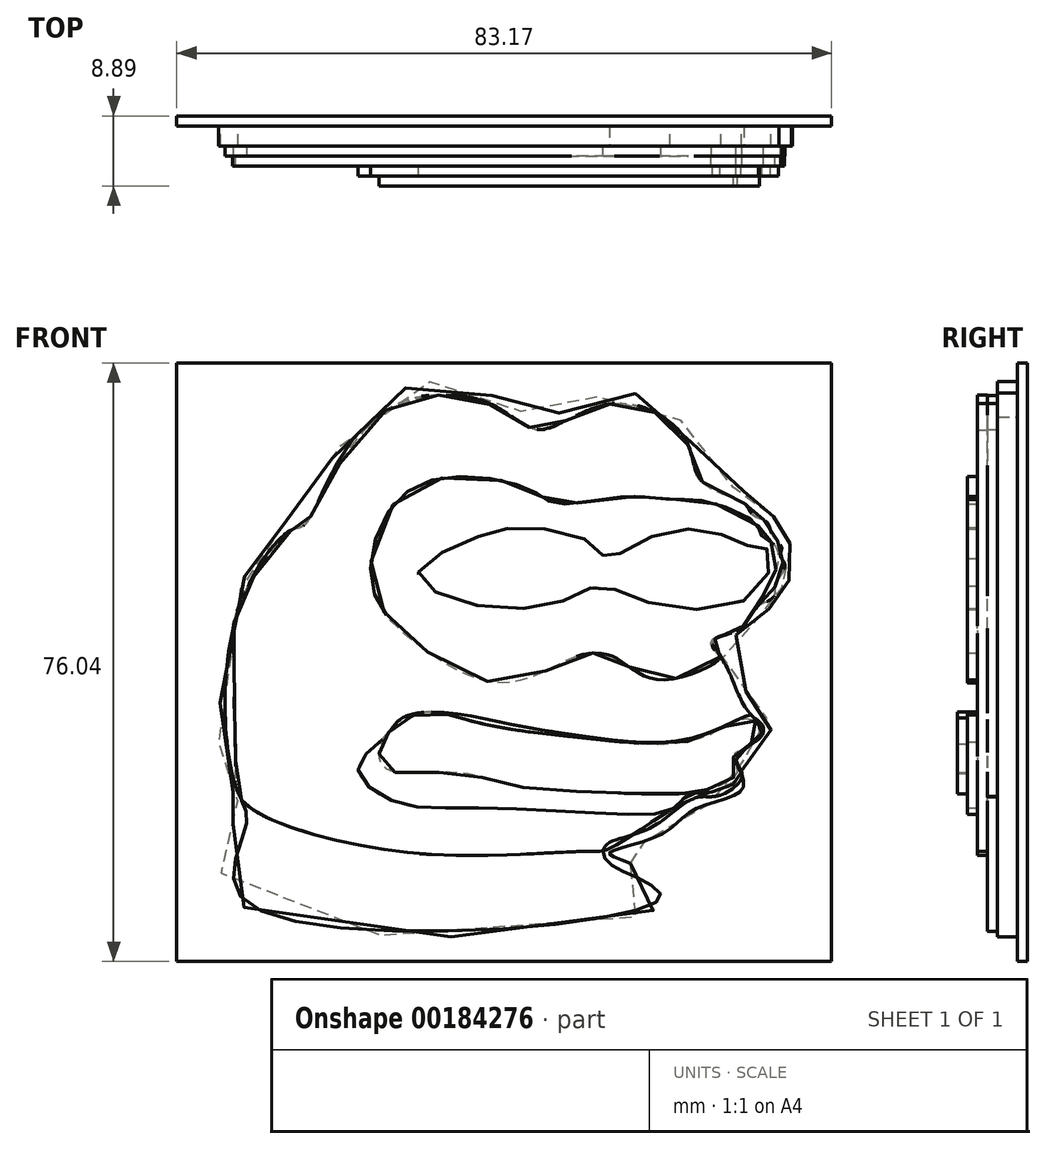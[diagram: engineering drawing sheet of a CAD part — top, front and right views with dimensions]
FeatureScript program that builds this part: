
annotation { "Feature Type Name" : "Feature", "Feature Type Description" : "" }
export const myFeature = defineFeature(function(context is Context, id is Id, definition is map)
    precondition{}
    {
        {
            var Q0;
            Q0=qCreatedBy(makeId("Front.planeOp"),FACE);
            var sketch = newSketch(context, id + "F0", { "sketchPlane" : qUnion([Q0])});
            skFitSpline(sketch, "E0", {"points": [v(8, -18.43) * mm, v(5.33, -17.05) * mm, v(11.68, -14.84) * mm, v(16.43, -11.4) * mm, v(22.25, -8.91) * mm, v(22.15, -5.68) * mm, v(25.7, -2.23) * mm, v(25.32, 0) * mm, v(24.4, 1.42) * mm, v(19.51, 9.3) * mm, v(23.44, 11.4) * mm, v(24.13, 12.87) * mm, v(26.85, 14.85) * mm, v(27, 16.2) * mm, v(28.38, 17.9) * mm, v(28.35, 20.42) * mm, v(28.25, 22.22) * mm, v(26.83, 23.31) * mm, v(26.67, 25.3) * mm, v(24.58, 26.28) * mm, v(23.94, 27.85) * mm, v(17.93, 31.16) * mm, v(13.41, 39.13) * mm, v(4.14, 40.92) * mm, v(-3.5, 38.31) * mm, v(-12.1, 42.14) * mm, v(-24.11, 40.06) * mm, v(-33.8, 27) * mm, v(-38.3, 22.43) * mm, v(-41.8, 15.7) * mm, v(-43.63, -8.1) * mm, v(-41.95, -9.82) * mm, v(-41.96, -10.5) * mm, v(-42.26, -12.67) * mm, v(-42.26, -23.19) * mm, v(12.68, -23.19) * mm, v(8, -18.43) * mm]});
            skSolve(sketch);
        }
        {
            var Q0;
            Q0 = qSketchRegion(id + "F0", true);
            extrude(context, id + "F1", {"entities" : qUnion([Q0]), "depth" : 2.54 * mm});
        }
        {
            var Q0;
            Q0=makeQuery(id+"F1.opExtrude","CAP_FACE",FACE,{"disambiguationData":[OSD([sQuery(id+"F0.wireOp",EDGE,"E0")])],"isStart":false});
            var sketch = newSketch(context, id + "F2", { "sketchPlane" : qUnion([Q0])});
            skFitSpline(sketch, "E1", {"points": [v(-33.38, 24.65) * mm, v(-25.5, 37.37) * mm, v(-10.06, 40.08) * mm, v(-3.7, 36.7) * mm, v(5.5, 39.96) * mm, v(14.93, 35.51) * mm, v(17.07, 30.08) * mm, v(22.74, 27.06) * mm, v(23.51, 25.83) * mm, v(25.27, 24.96) * mm, v(26.1, 23.08) * mm, v(27.19, 21.72) * mm, v(27, 20.66) * mm, v(27.6, 19.47) * mm, v(26.38, 16.98) * mm, v(26.1, 15.4) * mm, v(23.77, 13.98) * mm, v(21.96, 11.45) * mm, v(18.34, 9.98) * mm, v(19.18, 8.31) * mm, v(21.94, 2.3) * mm, v(23.3, 0.49) * mm, v(24.81, -1.9) * mm, v(21.39, -4.97) * mm, v(22.16, -7.13) * mm, v(19.2, -9.8) * mm, v(16.09, -10.11) * mm, v(10.35, -13.98) * mm, v(4.86, -16.1) * mm, v(4.74, -17.82) * mm, v(8.67, -20.17) * mm, v(11.6, -23.06) * mm, v(-40.87, -23.34) * mm, v(-40.82, -13.42) * mm, v(-42.17, -8.63) * mm, v(-42.07, 12.99) * mm, v(-35.07, 23.98) * mm, v(-33.38, 24.65) * mm]});
            skSolve(sketch);
        }
        {
            var Q0;
            Q0 = qSketchRegion(id + "F2", true);
            extrude(context, id + "F3", {"entities" : qUnion([Q0]), "operationType" : NewBodyOperationType.ADD, "depth" : 1.27 * mm});
        }
        {
            var Q0;
            Q0=makeQuery(id+"F3.opExtrude","CAP_FACE",FACE,{"disambiguationData":[OSD([sQuery(id+"F2.wireOp",EDGE,"E1")])],"isStart":false});
            var sketch = newSketch(context, id + "F4", { "sketchPlane" : qUnion([Q0])});
            skFitSpline(sketch, "E2", {"points": [v(-41.45, -10.34) * mm, v(-29.72, -15.39) * mm, v(-12.36, -17.43) * mm, v(2.82, -16.88) * mm, v(4.5, -16.82) * mm, v(8.25, -14.78) * mm, v(15.37, -10.45) * mm, v(22.15, -6.99) * mm, v(21.35, -5.18) * mm, v(24.86, -1.48) * mm, v(23.04, 0.73) * mm, v(19.87, 7.07) * mm, v(18.27, 9.76) * mm, v(21.94, 11.43) * mm, v(23.57, 13.76) * mm, v(26.19, 15.53) * mm, v(26.4, 17.05) * mm, v(27.5, 19) * mm, v(27, 20.72) * mm, v(27.01, 22.06) * mm, v(25.92, 23.47) * mm, v(25.2, 25.03) * mm, v(23.32, 26.06) * mm, v(22.48, 27.26) * mm, v(17.08, 30.06) * mm, v(15.5, 34.2) * mm, v(11.65, 38.54) * mm, v(5.92, 40) * mm, v(0, 37.94) * mm, v(-3.92, 36.7) * mm, v(-8.45, 39.23) * mm, v(-15.47, 41.04) * mm, v(-23.54, 38.82) * mm, v(-31.7, 27.6) * mm, v(-33.56, 24.5) * mm, v(-34.9, 24.04) * mm, v(-40.63, 16.77) * mm, v(-42.5, 11.35) * mm, v(-42.42, 8.38) * mm, v(-42.35, 1.27) * mm, v(-42.21, -6.13) * mm, v(-41.45, -10.34) * mm]});
            skSolve(sketch);
        }
        {
            var Q0;
            Q0 = qSketchRegion(id + "F4", true);
            extrude(context, id + "F5", {"entities" : qUnion([Q0]), "operationType" : NewBodyOperationType.ADD, "depth" : 1.27 * mm});
        }
        {
            var Q0;
            Q0=makeQuery(id+"F5.opExtrude","CAP_FACE",FACE,{"disambiguationData":[OSD([sQuery(id+"F4.wireOp",EDGE,"E2")])],"isStart":false});
            var sketch = newSketch(context, id + "F6", { "sketchPlane" : qUnion([Q0])});
            skFitSpline(sketch, "E3", {"points": [v(23.29, 0.46) * mm, v(16.19, -2.4) * mm, v(3.67, -2.47) * mm, v(-5.95, -0.99) * mm, v(-15.7, 0.76) * mm, v(-21.1, 0) * mm, v(-23.31, -2.47) * mm, v(-26.6, -6.24) * mm, v(-22.3, -10.48) * mm, v(-11.74, -11.35) * mm, v(6.43, -12.16) * mm, v(13.48, -11.4) * mm, v(15.25, -9.74) * mm, v(17.94, -9.4) * mm, v(22.02, -7.32) * mm, v(21.38, -5.08) * mm, v(24.65, -1.84) * mm, v(23.81, 0) * mm, v(23.29, 0.46) * mm]});
            skFitSpline(sketch, "E4", {"points": [v(19.35, 7.8) * mm, v(11.88, 4.9) * mm, v(6.31, 7.56) * mm, v(1.42, 7.98) * mm, v(-8.04, 4.51) * mm, v(-19.98, 10.14) * mm, v(-24.91, 17.22) * mm, v(-21.75, 27.64) * mm, v(-12.44, 30.74) * mm, v(-4, 28.67) * mm, v(-1.58, 27.31) * mm, v(7.38, 28.16) * mm, v(13.43, 27.83) * mm, v(17.85, 27.53) * mm, v(24.29, 24.4) * mm, v(24.26, 23.56) * mm, v(26.12, 22.2) * mm, v(26.64, 19.53) * mm, v(25.45, 16.84) * mm, v(24.05, 14.14) * mm, v(21.4, 11.13) * mm, v(18.7, 10.1) * mm, v(18.56, 8.79) * mm, v(19.35, 7.8) * mm]});
            skFitSpline(sketch, "E5", {"points": [v(-18.94, 18.58) * mm, v(-12.22, 22.74) * mm, v(-5.9, 24.26) * mm, v(3.47, 22.02) * mm, v(4.99, 20.34) * mm, v(10.19, 22.9) * mm, v(18.43, 23.7) * mm, v(23.4, 21.86) * mm, v(25.47, 21.38) * mm, v(23.95, 16.02) * mm, v(10.43, 14.66) * mm, v(4.03, 16.84) * mm, v(-1.18, 14.74) * mm, v(-13.74, 14.9) * mm, v(-18.94, 18.58) * mm]});
            skSolve(sketch);
        }
        {
            var Q0;
            Q0 = qSketchRegion(id + "F6", true);
            extrude(context, id + "F7", {"entities" : qUnion([Q0]), "operationType" : NewBodyOperationType.ADD, "depth" : 1.27 * mm});
        }
        {
            var Q0;
            Q0=makeQuery(id+"F7.opExtrude","CAP_FACE",FACE,{"disambiguationData":[OSD([sQuery(id+"F6.wireOp",EDGE,"E4")])],"isStart":false});
            var sketch = newSketch(context, id + "F8", { "sketchPlane" : qUnion([Q0])});
            skFitSpline(sketch, "E6", {"points": [v(-21.96, -6.83) * mm, v(-23.86, -5.18) * mm, v(-23.55, -2.7) * mm, v(-22.15, -1.3) * mm, v(-18.6, 0.72) * mm, v(-13.45, 0) * mm, v(-8.75, -1.12) * mm, v(-2.84, -1.94) * mm, v(5.29, -2.83) * mm, v(12.28, -3.21) * mm, v(18.25, -1.94) * mm, v(23.2, 0) * mm, v(24.34, -1.69) * mm, v(22.37, -3.78) * mm, v(21.04, -4.8) * mm, v(21.55, -6.52) * mm, v(19.96, -8.3) * mm, v(16.91, -9.18) * mm, v(14.3, -9.56) * mm, v(3.38, -9.37) * mm, v(-7.6, -8.42) * mm, v(-13.96, -6.9) * mm, v(-21.96, -6.83) * mm]});
            skSolve(sketch);
        }
        {
            var Q0;
            Q0 = qSketchRegion(id + "F8", true);
            extrude(context, id + "F9", {"entities" : qUnion([Q0]), "operationType" : NewBodyOperationType.ADD, "depth" : 1.27 * mm});
        }
        {
            var Q0;
            Q0=makeQuery(id+"F1.opExtrude","CAP_FACE",FACE,{"disambiguationData":[OSD([sQuery(id+"F0.wireOp",EDGE,"E0")])],"isStart":true});
            var sketch = newSketch(context, id + "F10", { "sketchPlane" : qUnion([Q0])});
            skLineSegment(sketch, "E7.bottom", {"start": v(-33.51, 45.15) * mm, "end": v(49.66, 45.15) * mm});
            skLineSegment(sketch, "E7.top", {"start": v(-33.51, -30.89) * mm, "end": v(49.66, -30.89) * mm});
            skLineSegment(sketch, "E7.left", {"start": v(-33.51, 45.15) * mm, "end": v(-33.51, -30.89) * mm});
            skLineSegment(sketch, "E7.right", {"start": v(49.66, 45.15) * mm, "end": v(49.66, -30.89) * mm});
            skSolve(sketch);
        }
        {
            var Q0;
            Q0 = qSketchRegion(id + "F10", true);
            extrude(context, id + "F11", {"entities" : qUnion([Q0]), "operationType" : NewBodyOperationType.ADD, "depth" : 1.27 * mm});
        }
    });
